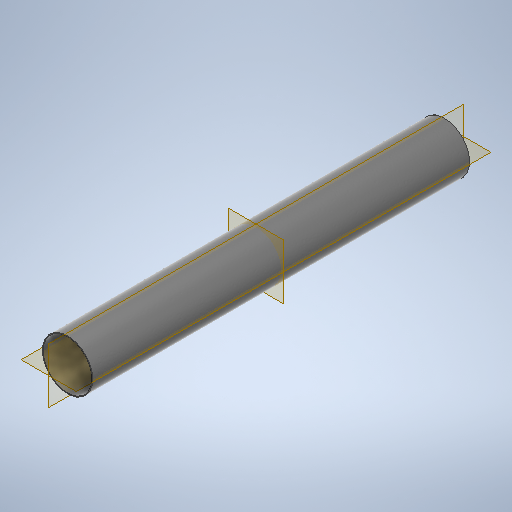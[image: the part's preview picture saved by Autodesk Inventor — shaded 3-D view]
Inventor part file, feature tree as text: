
AUTODESK INVENTOR PART (.ipt)
format: ipt  version: 2025.2 (Build 292293000, 293)  size: 272,384 bytes
history: native  units: mm
features: extrude x1, sketch x1
ambient origin geometry x8: Origin, YZ Plane, XZ Plane, XY Plane, X Axis, Y Axis, Z Axis, Center Point
bodies: Solid1 (feature_tree)
feature tree (2):
  extrude  "Extrusion1"  Depth=750.0mm
  sketch  "Sketch1"  dims[d0=100.0mm d1=97.0mm d2=750.0mm d3=0.0mm]
